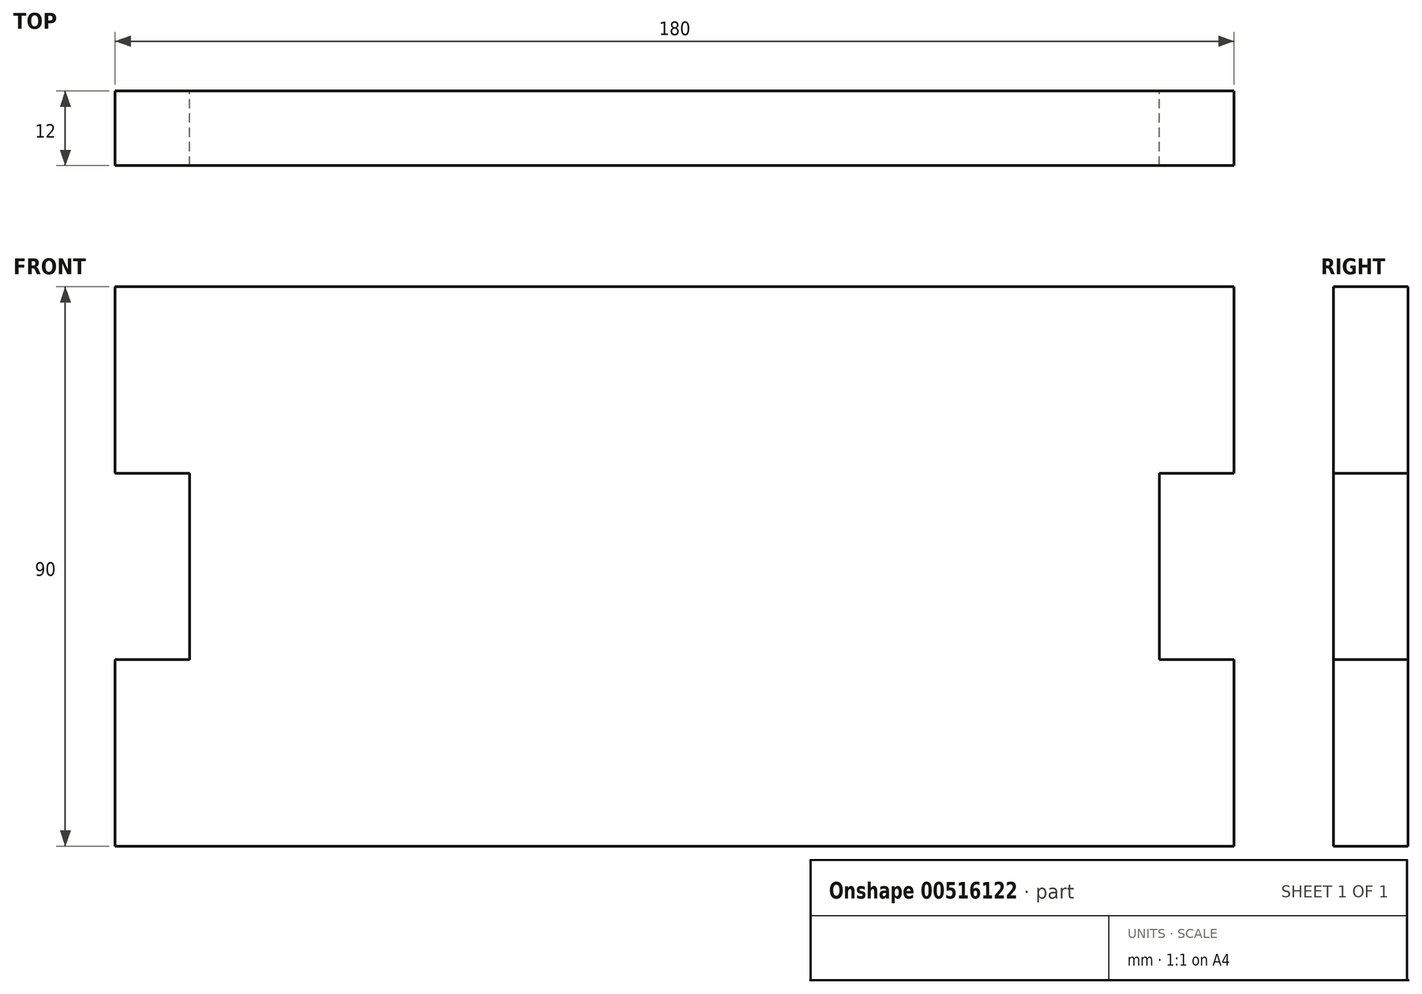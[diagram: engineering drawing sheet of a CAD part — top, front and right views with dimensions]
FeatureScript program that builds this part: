
annotation { "Feature Type Name" : "Feature", "Feature Type Description" : "" }
export const myFeature = defineFeature(function(context is Context, id is Id, definition is map)
    precondition{}
    {
        {
            var Q0;
            Q0=qCreatedBy(makeId("Front.planeOp"),FACE);
            var sketch = newSketch(context, id + "F0", { "sketchPlane" : qUnion([Q0])});
            skLineSegment(sketch, "E0", {"start": v(0, 0) * mm, "end": v(0, 30) * mm});
            skLineSegment(sketch, "E1", {"start": v(0, 30) * mm, "end": v(12, 30) * mm});
            skLineSegment(sketch, "E2", {"start": v(12, 30) * mm, "end": v(12, 60) * mm});
            skLineSegment(sketch, "E3", {"start": v(12, 60) * mm, "end": v(0, 60) * mm});
            skLineSegment(sketch, "E4", {"start": v(0, 60) * mm, "end": v(0, 90) * mm});
            skLineSegment(sketch, "E5", {"start": v(0, 90) * mm, "end": v(90, 90) * mm});
            skLineSegment(sketch, "E6", {"start": v(90, 90) * mm, "end": v(90, 0) * mm, "construction": true});
            skLineSegment(sketch, "E7", {"start": v(90, 0) * mm, "end": v(0, 0) * mm});
            skLineSegment(sketch, "E8.MirrorCS", {"start": v(180, 30) * mm, "end": v(168, 30) * mm});
            skLineSegment(sketch, "E9.MirrorCS", {"start": v(168, 30) * mm, "end": v(168, 60) * mm});
            skLineSegment(sketch, "E10.MirrorCS", {"start": v(90, 0) * mm, "end": v(180, 0) * mm});
            skLineSegment(sketch, "E11.MirrorCS", {"start": v(180, 90) * mm, "end": v(90, 90) * mm});
            skLineSegment(sketch, "E12.MirrorCS", {"start": v(180, 0) * mm, "end": v(180, 30) * mm});
            skLineSegment(sketch, "E13.MirrorCS", {"start": v(180, 60) * mm, "end": v(180, 90) * mm});
            skLineSegment(sketch, "E14.MirrorCS", {"start": v(168, 60) * mm, "end": v(180, 60) * mm});
            skSolve(sketch);
        }
        {
            var Q0;
            Q0=makeQuery(id+"F0.imprint","IMPRINT",FACE,{"disambiguationData":[TD([[makeQuery(id+"F0.imprint","IMPRINT",EDGE,{"derivedFrom":sQuery(id+"F0.wireOp",EDGE,"E0")}),-1.0]])]});
            extrude(context, id + "F1", {"entities" : qUnion([Q0]), "endBound" : BoundingType.SYMMETRIC, "depth" : 12 * mm, "offsetDistance" : 25 * mm});
        }
    });
